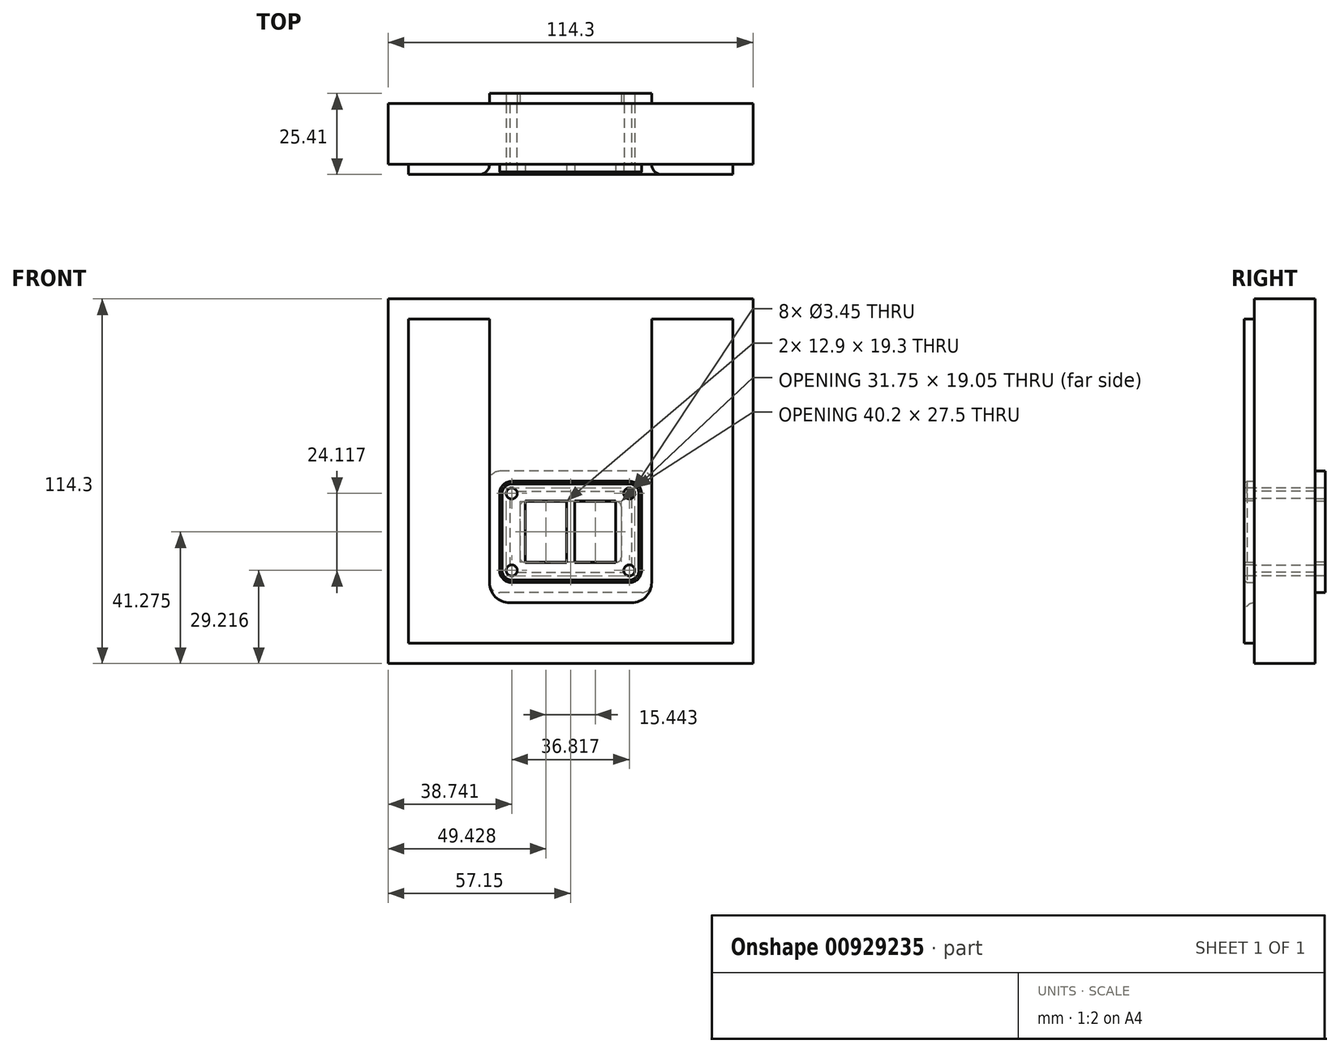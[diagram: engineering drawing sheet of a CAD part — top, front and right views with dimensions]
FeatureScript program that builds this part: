
annotation { "Feature Type Name" : "Feature", "Feature Type Description" : "" }
export const myFeature = defineFeature(function(context is Context, id is Id, definition is map)
    precondition{}
    {
        {
            var Q0;
            Q0=qCreatedBy(makeId("Front.planeOp"),FACE);
            var sketch = newSketch(context, id + "F0", { "sketchPlane" : qUnion([Q0])});
            skLineSegment(sketch, "E0.bottom", {"start": v(-57.15, -57.15) * mm, "end": v(57.15, -57.15) * mm});
            skLineSegment(sketch, "E0.top", {"start": v(-57.15, 57.15) * mm, "end": v(57.15, 57.15) * mm});
            skLineSegment(sketch, "E0.left", {"start": v(-57.15, -57.15) * mm, "end": v(-57.15, 57.15) * mm});
            skLineSegment(sketch, "E0.right", {"start": v(57.15, -57.15) * mm, "end": v(57.15, 57.15) * mm});
            skSolve(sketch);
        }
        {
            var Q0;
            Q0 = qSketchRegion(id + "F0", true);
            extrude(context, id + "F1", {"entities" : qUnion([Q0]), "oppositeDirection" : true, "depth" : 19.05 * mm, "offsetDistance" : 25.4 * mm});
        }
        {
            var Q0;
            Q0=qCreatedBy(makeId("Front.planeOp"),FACE);
            var sketch = newSketch(context, id + "F2", { "sketchPlane" : qUnion([Q0])});
            skLineSegment(sketch, "E1.top", {"start": v(-50.8, -50.8) * mm, "end": v(50.8, -50.8) * mm});
            skLineSegment(sketch, "E1.left", {"start": v(-50.8, 50.8) * mm, "end": v(-50.8, -50.8) * mm});
            skLineSegment(sketch, "E1.right", {"start": v(50.8, 50.8) * mm, "end": v(50.8, -50.8) * mm});
            skLineSegment(sketch, "E2.top", {"start": v(-19.05, -38.1) * mm, "end": v(19.05, -38.1) * mm});
            skLineSegment(sketch, "E2.left", {"start": v(-25.4, 50.8) * mm, "end": v(-25.4, -31.75) * mm});
            skLineSegment(sketch, "E2.right", {"start": v(25.4, 50.8) * mm, "end": v(25.4, -31.75) * mm});
            skPoint(sketch, "E3.visualSharp", {"position": v(-25.4, -38.1) * mm});
            skArc(sketch, "E3.filletArc", {"start": v(-25.4, -31.75) * mm, "mid": v(-23.54, -36.24) * mm, "end": v(-19.05, -38.1) * mm});
            skPoint(sketch, "E4.visualSharp", {"position": v(25.4, -38.1) * mm});
            skArc(sketch, "E4.filletArc", {"start": v(19.05, -38.1) * mm, "mid": v(23.54, -36.24) * mm, "end": v(25.4, -31.75) * mm});
            skLineSegment(sketch, "E5", {"start": v(-50.8, 50.8) * mm, "end": v(-25.4, 50.8) * mm});
            skLineSegment(sketch, "E6", {"start": v(25.4, 50.8) * mm, "end": v(50.8, 50.8) * mm});
            skSolve(sketch);
        }
        {
            var Q0;
            Q0 = qSketchRegion(id + "F2", true);
            extrude(context, id + "F3", {"entities" : qUnion([Q0]), "depth" : 3.17 * mm, "offsetDistance" : 25.4 * mm});
        }
        {
            var Q0;
            Q0=makeQuery(id+"F3.opExtrude","CAP_EDGE",EDGE,{"disambiguationData":[OSD([sQuery(id+"F2.wireOp",EDGE,"E2.left")])],"isStart":false});
            fillet(context, id + "F4", {"entities" : qUnion([Q0]), "radius" : 3.17 * mm, "tangentPropagation" : true, "allowEdgeOverflow" : false});
        }
        {
            var Q0;
            Q0=qCreatedBy(makeId("Front.planeOp"),FACE);
            var sketch = newSketch(context, id + "F5", { "sketchPlane" : qUnion([Q0])});
            skLineSegment(sketch, "E7.bottom", {"start": v(-19.05, -3.17) * mm, "end": v(19.05, -3.17) * mm});
            skLineSegment(sketch, "E7.top", {"start": v(-19.05, -28.58) * mm, "end": v(19.05, -28.58) * mm});
            skLineSegment(sketch, "E7.left", {"start": v(-19.05, -3.17) * mm, "end": v(-19.05, -28.58) * mm});
            skLineSegment(sketch, "E7.right", {"start": v(19.05, -3.17) * mm, "end": v(19.05, -28.58) * mm});
            skSolve(sketch);
        }
        {
            var Q0;
            Q0 = qSketchRegion(id + "F5", true);
            extrude(context, id + "F6", {"entities" : qUnion([Q0]), "operationType" : NewBodyOperationType.REMOVE, "endBound" : BoundingType.THROUGH_ALL, "oppositeDirection" : true, "depth" : 25.4 * mm, "offsetDistance" : 25.4 * mm});
        }
        {
            var Q0;
            Q0=qCreatedBy(makeId("Front.planeOp"),FACE);
            var sketch = newSketch(context, id + "F7", { "sketchPlane" : qUnion([Q0])});
            skLineSegment(sketch, "E8.bottom", {"start": v(-18.4, 0) * mm, "end": v(18.4, 0) * mm});
            skLineSegment(sketch, "E8.top", {"start": v(-18.4, -31.75) * mm, "end": v(18.4, -31.75) * mm});
            skLineSegment(sketch, "E8.left", {"start": v(-22.23, -3.82) * mm, "end": v(-22.23, -27.93) * mm});
            skLineSegment(sketch, "E8.right", {"start": v(22.23, -3.82) * mm, "end": v(22.23, -27.93) * mm});
            skPoint(sketch, "E9.visualSharp", {"position": v(-22.23, 0) * mm});
            skArc(sketch, "E9.filletArc", {"start": v(-18.4, 0) * mm, "mid": v(-21.1, -1.12) * mm, "end": v(-22.23, -3.82) * mm});
            skPoint(sketch, "E10.visualSharp", {"position": v(22.22, 0) * mm});
            skArc(sketch, "E10.filletArc", {"start": v(22.23, -3.82) * mm, "mid": v(21.1, -1.12) * mm, "end": v(18.4, 0) * mm});
            skPoint(sketch, "E11.visualSharp", {"position": v(22.23, -31.75) * mm});
            skArc(sketch, "E11.filletArc", {"start": v(18.4, -31.75) * mm, "mid": v(21.1, -30.63) * mm, "end": v(22.23, -27.93) * mm});
            skPoint(sketch, "E12.visualSharp", {"position": v(-22.23, -31.75) * mm});
            skArc(sketch, "E12.filletArc", {"start": v(-22.23, -27.93) * mm, "mid": v(-21.1, -30.63) * mm, "end": v(-18.4, -31.75) * mm});
            skSolve(sketch);
        }
        {
            var Q0;
            Q0 = qSketchRegion(id + "F7", true);
            extrude(context, id + "F8", {"entities" : qUnion([Q0]), "depth" : 3.17 * mm, "offsetDistance" : 25.4 * mm});
        }
        {
            var Q0;
            Q0=makeQuery(id+"F8.opExtrude","CAP_FACE",FACE,{"disambiguationData":[OSD([sQuery(id+"F7.wireOp",EDGE,"E8.bottom"),sQuery(id+"F7.wireOp",EDGE,"E8.top"),sQuery(id+"F7.wireOp",EDGE,"E8.left"),sQuery(id+"F7.wireOp",EDGE,"E8.right"),sQuery(id+"F7.wireOp",EDGE,"E9.filletArc"),sQuery(id+"F7.wireOp",EDGE,"E10.filletArc"),sQuery(id+"F7.wireOp",EDGE,"E11.filletArc"),sQuery(id+"F7.wireOp",EDGE,"E12.filletArc")])],"isStart":false});
            chamfer(context, id + "F9", {"entities" : qUnion([Q0]), "width" : 0.8 * mm, "tangentPropagation" : true});
        }
        {
            var Q0;
            Q0=makeQuery(id+"F8.opExtrude","CAP_FACE",FACE,{"disambiguationData":[OSD([sQuery(id+"F7.wireOp",EDGE,"E8.bottom"),sQuery(id+"F7.wireOp",EDGE,"E8.top"),sQuery(id+"F7.wireOp",EDGE,"E8.left"),sQuery(id+"F7.wireOp",EDGE,"E8.right"),sQuery(id+"F7.wireOp",EDGE,"E9.filletArc"),sQuery(id+"F7.wireOp",EDGE,"E10.filletArc"),sQuery(id+"F7.wireOp",EDGE,"E11.filletArc"),sQuery(id+"F7.wireOp",EDGE,"E12.filletArc")])],"isStart":false});
            var sketch = newSketch(context, id + "F10", { "sketchPlane" : qUnion([Q0])});
            skLineSegment(sketch, "E13.bottom", {"start": v(-14.17, -6.22) * mm, "end": v(-1.27, -6.22) * mm});
            skLineSegment(sketch, "E13.top", {"start": v(-14.17, -25.53) * mm, "end": v(-1.27, -25.53) * mm});
            skLineSegment(sketch, "E13.left", {"start": v(-14.17, -6.22) * mm, "end": v(-14.17, -25.53) * mm});
            skLineSegment(sketch, "E13.right", {"start": v(-1.27, -6.22) * mm, "end": v(-1.27, -25.53) * mm});
            skLineSegment(sketch, "E14.bottom", {"start": v(-14.45, -5.38) * mm, "end": v(-1.02, -5.38) * mm, "construction": true});
            skLineSegment(sketch, "E14.top", {"start": v(-14.45, -26.4) * mm, "end": v(-1.02, -26.4) * mm, "construction": true});
            skLineSegment(sketch, "E14.left", {"start": v(-15.24, -6.18) * mm, "end": v(-15.24, -25.6) * mm, "construction": true});
            skLineSegment(sketch, "E14.right", {"start": v(-0.23, -6.18) * mm, "end": v(-0.23, -25.6) * mm, "construction": true});
            skPoint(sketch, "E15.visualSharp", {"position": v(-15.24, -5.38) * mm});
            skArc(sketch, "E15.filletArc", {"start": v(-14.45, -5.38) * mm, "mid": v(-15, -5.62) * mm, "end": v(-15.24, -6.18) * mm, "construction": true});
            skPoint(sketch, "E16.visualSharp", {"position": v(-0.23, -5.38) * mm});
            skArc(sketch, "E16.filletArc", {"start": v(-0.23, -6.18) * mm, "mid": v(-0.46, -5.62) * mm, "end": v(-1.02, -5.38) * mm, "construction": true});
            skPoint(sketch, "E17.visualSharp", {"position": v(-0.23, -26.4) * mm});
            skArc(sketch, "E17.filletArc", {"start": v(-1.02, -26.4) * mm, "mid": v(-0.46, -26.16) * mm, "end": v(-0.23, -25.6) * mm, "construction": true});
            skPoint(sketch, "E18.visualSharp", {"position": v(-15.24, -26.4) * mm});
            skArc(sketch, "E18.filletArc", {"start": v(-15.24, -25.6) * mm, "mid": v(-15, -26.16) * mm, "end": v(-14.45, -26.4) * mm, "construction": true});
            skArc(sketch, "E19.MirrorCS", {"start": v(1.02, -26.4) * mm, "mid": v(0.46, -26.16) * mm, "end": v(0.23, -25.6) * mm, "construction": true});
            skArc(sketch, "E20.MirrorCS", {"start": v(14.45, -5.38) * mm, "mid": v(15, -5.62) * mm, "end": v(15.24, -6.18) * mm, "construction": true});
            skArc(sketch, "E21.MirrorCS", {"start": v(0.23, -6.18) * mm, "mid": v(0.46, -5.62) * mm, "end": v(1.02, -5.38) * mm, "construction": true});
            skArc(sketch, "E22.MirrorCS", {"start": v(15.24, -25.6) * mm, "mid": v(15, -26.16) * mm, "end": v(14.45, -26.4) * mm, "construction": true});
            skPoint(sketch, "E23.MirrorP", {"position": v(15.24, -26.4) * mm});
            skLineSegment(sketch, "E24.MirrorCS", {"start": v(14.17, -6.22) * mm, "end": v(14.17, -25.53) * mm});
            skLineSegment(sketch, "E25.MirrorCS", {"start": v(14.17, -25.53) * mm, "end": v(1.27, -25.53) * mm});
            skLineSegment(sketch, "E26.MirrorCS", {"start": v(1.27, -6.22) * mm, "end": v(1.27, -25.53) * mm});
            skPoint(sketch, "E27.MirrorP", {"position": v(0.23, -26.4) * mm});
            skLineSegment(sketch, "E28.MirrorCS", {"start": v(14.17, -6.22) * mm, "end": v(1.27, -6.22) * mm});
            skPoint(sketch, "E29.MirrorP", {"position": v(15.24, -5.38) * mm});
            skLineSegment(sketch, "E30.MirrorCS", {"start": v(14.45, -26.4) * mm, "end": v(1.02, -26.4) * mm, "construction": true});
            skPoint(sketch, "E31.MirrorP", {"position": v(0.23, -5.38) * mm});
            skLineSegment(sketch, "E32.MirrorCS", {"start": v(15.24, -6.18) * mm, "end": v(15.24, -25.6) * mm, "construction": true});
            skLineSegment(sketch, "E33.MirrorCS", {"start": v(14.45, -5.38) * mm, "end": v(1.02, -5.38) * mm, "construction": true});
            skLineSegment(sketch, "E34.MirrorCS", {"start": v(0.23, -6.18) * mm, "end": v(0.23, -25.6) * mm, "construction": true});
            skSolve(sketch);
        }
        {
            var Q0;
            Q0 = qSketchRegion(id + "F10", true);
            extrude(context, id + "F11", {"entities" : qUnion([Q0]), "operationType" : NewBodyOperationType.REMOVE, "endBound" : BoundingType.THROUGH_ALL, "oppositeDirection" : true, "depth" : 25.4 * mm, "offsetDistance" : 25.4 * mm});
        }
        {
            var Q0;
            Q0=makeQuery(id+"F10.imprint","IMPRINT",FACE,{"disambiguationData":[TD([[makeQuery(id+"F10.imprint","IMPRINT",EDGE,{"derivedFrom":sQuery(id+"F10.wireOp",EDGE,"E13.bottom")}),1.0]])]});
            var sketch = newSketch(context, id + "F12", { "sketchPlane" : qUnion([Q0])});
            skCircle(sketch, "E35", {"center": v(-18.4, -3.82) * mm, "radius": 1.73 * mm});
            skCircle(sketch, "E36", {"center": v(-18.4, -3.82) * mm, "radius": 3.02 * mm, "construction": true});
            skCircle(sketch, "E37", {"center": v(-18.4, -27.93) * mm, "radius": 1.73 * mm});
            skCircle(sketch, "E38", {"center": v(-18.4, -27.93) * mm, "radius": 3.02 * mm, "construction": true});
            skCircle(sketch, "E39.MirrorC", {"center": v(18.4, -3.82) * mm, "radius": 1.73 * mm});
            skCircle(sketch, "E40.MirrorC", {"center": v(18.4, -3.82) * mm, "radius": 3.02 * mm, "construction": true});
            skCircle(sketch, "E41.MirrorC", {"center": v(18.4, -27.93) * mm, "radius": 1.73 * mm});
            skCircle(sketch, "E42.MirrorC", {"center": v(18.4, -27.93) * mm, "radius": 3.02 * mm, "construction": true});
            skSolve(sketch);
        }
        {
            var Q0;
            Q0 = qSketchRegion(id + "F12", true);
            extrude(context, id + "F13", {"entities" : qUnion([Q0]), "operationType" : NewBodyOperationType.REMOVE, "endBound" : BoundingType.THROUGH_ALL, "oppositeDirection" : true, "depth" : 25.4 * mm, "offsetDistance" : 25.4 * mm});
        }
        {
            var Q0;
            Q0=makeQuery(id+"F1.opExtrude","CAP_FACE",FACE,{"disambiguationData":[OSD([sQuery(id+"F0.wireOp",EDGE,"E0.bottom"),sQuery(id+"F0.wireOp",EDGE,"E0.top"),sQuery(id+"F0.wireOp",EDGE,"E0.left"),sQuery(id+"F0.wireOp",EDGE,"E0.right")])],"isStart":false});
            var sketch = newSketch(context, id + "F14", { "sketchPlane" : qUnion([Q0])});
            skLineSegment(sketch, "E43.bottom", {"start": v(-22.22, 3.17) * mm, "end": v(22.23, 3.18) * mm});
            skLineSegment(sketch, "E43.top", {"start": v(-22.22, -34.92) * mm, "end": v(22.23, -34.92) * mm});
            skLineSegment(sketch, "E43.left", {"start": v(-25.4, 0) * mm, "end": v(-25.4, -31.75) * mm});
            skLineSegment(sketch, "E43.right", {"start": v(25.4, 0) * mm, "end": v(25.4, -31.75) * mm});
            skPoint(sketch, "E44.visualSharp", {"position": v(25.4, 3.18) * mm});
            skArc(sketch, "E44.filletArc", {"start": v(25.4, 0) * mm, "mid": v(24.47, 2.25) * mm, "end": v(22.23, 3.18) * mm});
            skPoint(sketch, "E45.visualSharp", {"position": v(-25.4, 3.17) * mm});
            skArc(sketch, "E45.filletArc", {"start": v(-22.22, 3.17) * mm, "mid": v(-24.47, 2.25) * mm, "end": v(-25.4, 0) * mm});
            skPoint(sketch, "E46.visualSharp", {"position": v(-25.4, -34.92) * mm});
            skArc(sketch, "E46.filletArc", {"start": v(-25.4, -31.75) * mm, "mid": v(-24.47, -34) * mm, "end": v(-22.22, -34.92) * mm});
            skPoint(sketch, "E47.visualSharp", {"position": v(25.4, -34.92) * mm});
            skArc(sketch, "E47.filletArc", {"start": v(22.23, -34.92) * mm, "mid": v(24.47, -34) * mm, "end": v(25.4, -31.75) * mm});
            skLineSegment(sketch, "E48.bottom", {"start": v(-14.29, -6.35) * mm, "end": v(14.29, -6.35) * mm});
            skLineSegment(sketch, "E48.top", {"start": v(-14.29, -25.4) * mm, "end": v(14.29, -25.4) * mm});
            skLineSegment(sketch, "E48.left", {"start": v(-15.88, -7.94) * mm, "end": v(-15.88, -23.81) * mm});
            skLineSegment(sketch, "E48.right", {"start": v(15.88, -7.94) * mm, "end": v(15.88, -23.81) * mm});
            skPoint(sketch, "E49.visualSharp", {"position": v(15.87, -6.35) * mm});
            skArc(sketch, "E49.filletArc", {"start": v(15.87, -7.94) * mm, "mid": v(15.41, -6.81) * mm, "end": v(14.29, -6.35) * mm});
            skPoint(sketch, "E50.visualSharp", {"position": v(15.88, -25.4) * mm});
            skArc(sketch, "E50.filletArc", {"start": v(14.29, -25.4) * mm, "mid": v(15.41, -24.94) * mm, "end": v(15.88, -23.81) * mm});
            skPoint(sketch, "E51.visualSharp", {"position": v(-15.88, -25.4) * mm});
            skArc(sketch, "E51.filletArc", {"start": v(-15.88, -23.81) * mm, "mid": v(-15.41, -24.94) * mm, "end": v(-14.29, -25.4) * mm});
            skPoint(sketch, "E52.visualSharp", {"position": v(-15.88, -6.35) * mm});
            skArc(sketch, "E52.filletArc", {"start": v(-14.29, -6.35) * mm, "mid": v(-15.41, -6.81) * mm, "end": v(-15.88, -7.94) * mm});
            skCircle(sketch, "E53", {"center": v(-18.4, -3.82) * mm, "radius": 1.73 * mm});
            skCircle(sketch, "E54", {"center": v(-18.4, -27.93) * mm, "radius": 1.73 * mm});
            skCircle(sketch, "E55", {"center": v(18.4, -3.82) * mm, "radius": 1.73 * mm});
            skCircle(sketch, "E56", {"center": v(18.4, -27.93) * mm, "radius": 1.73 * mm});
            skSolve(sketch);
        }
        {
            var Q0;
            Q0 = qSketchRegion(id + "F14", true);
            extrude(context, id + "F15", {"entities" : qUnion([Q0]), "depth" : 3.17 * mm, "offsetDistance" : 25.4 * mm});
        }
    });
